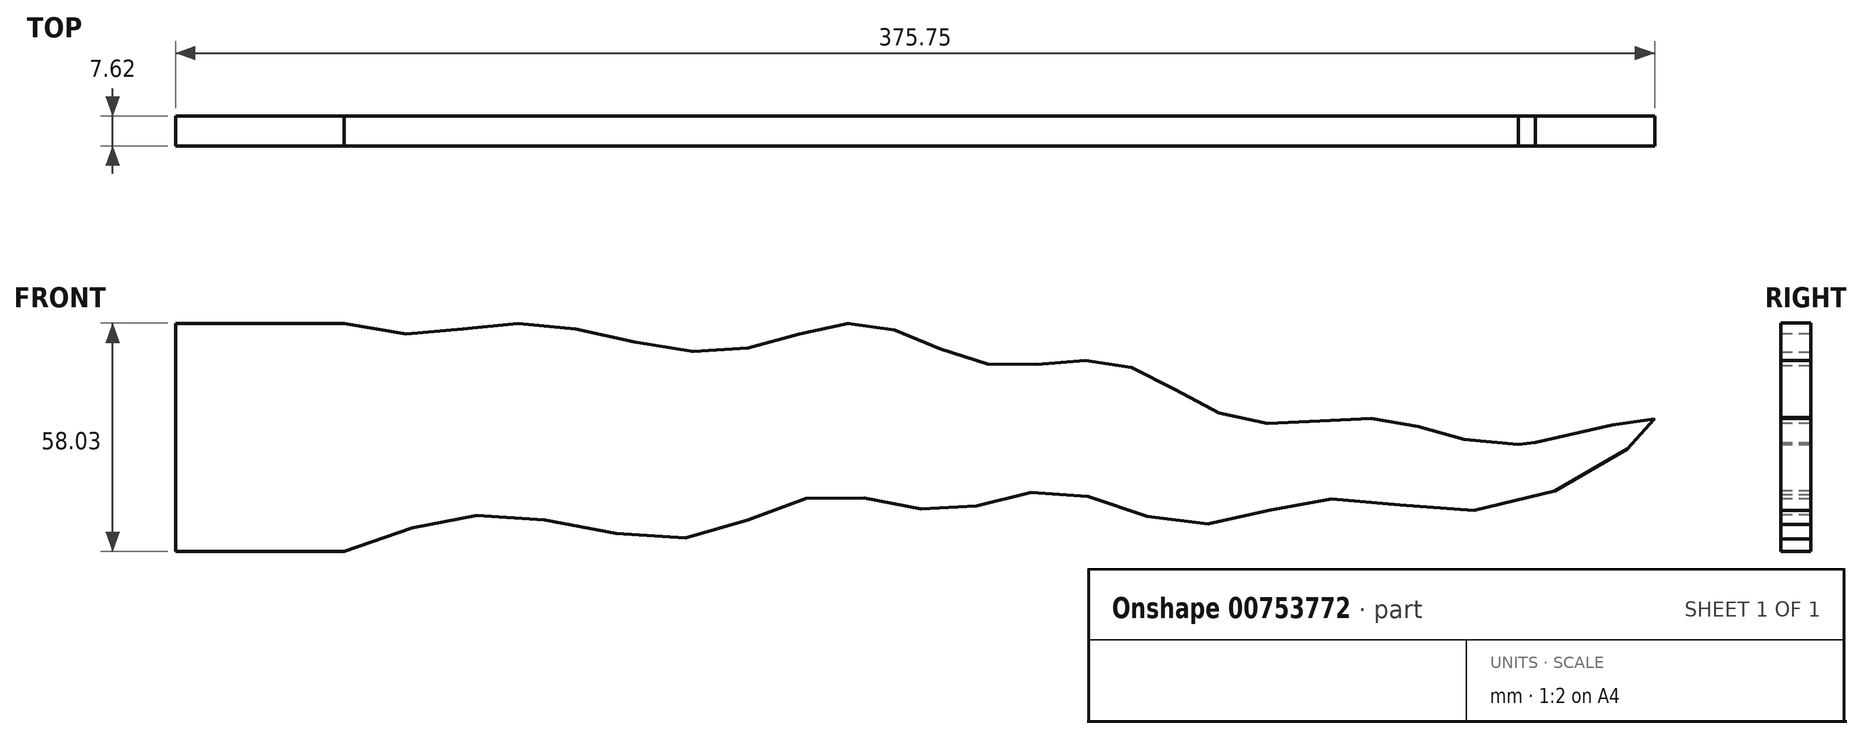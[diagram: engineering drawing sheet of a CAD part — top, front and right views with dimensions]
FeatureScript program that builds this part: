
annotation { "Feature Type Name" : "Feature", "Feature Type Description" : "" }
export const myFeature = defineFeature(function(context is Context, id is Id, definition is map)
    precondition{}
    {
        {
            var Q0;
            Q0=qCreatedBy(makeId("Front.planeOp"),FACE);
            var sketch = newSketch(context, id + "F0", { "sketchPlane" : qUnion([Q0])});
            skLineSegment(sketch, "E0.bottom", {"start": v(-130.14, 24.38) * mm, "end": v(-87.36, 24.38) * mm});
            skLineSegment(sketch, "E0.top", {"start": v(-130.14, -33.6) * mm, "end": v(-87.36, -33.6) * mm});
            skLineSegment(sketch, "E0.left", {"start": v(-130.14, 24.38) * mm, "end": v(-130.14, -33.6) * mm});
            skLineSegment(sketch, "E0.right", {"start": v(-87.36, 24.38) * mm, "end": v(-87.36, -33.6) * mm});
            skFitSpline(sketch, "E1", {"points": [v(-87.36, 24.38) * mm, v(-40.16, 24.38) * mm, v(7.86, 17.06) * mm, v(44.49, 24.38) * mm, v(76.3, 14.02) * mm, v(109.24, 14.24) * mm, v(139.64, 0) * mm, v(176.53, 0) * mm, v(210.97, -6.4) * mm, v(245.52, 0) * mm, v(211.78, -21.29) * mm, v(162.57, -20.33) * mm, v(127, -26.67) * mm, v(93.39, -18.18) * mm, v(65.16, -23.2) * mm, v(34.72, -19.34) * mm, v(0, -30.06) * mm, v(-45.62, -24.38) * mm, v(-87.36, -33.6) * mm], "startDerivative": vector(867.54, -301.74) * mm, "endDerivative": vector(-762.56, -288.29) * mm});
            skLineSegment(sketch, "E2.bottom", {"start": v(-130.14, 0) * mm, "end": v(-130.14, 0) * mm});
            skLineSegment(sketch, "E2.top", {"start": v(-130.14, -19) * mm, "end": v(-130.14, -19) * mm});
            skLineSegment(sketch, "E2.left", {"start": v(-130.14, 0) * mm, "end": v(-130.14, -19) * mm});
            skLineSegment(sketch, "E2.right", {"start": v(-130.14, 0) * mm, "end": v(-130.14, -19) * mm});
            skLineSegment(sketch, "E3", {"start": v(210.97, -6.4) * mm, "end": v(234, -3.99) * mm});
            skSolve(sketch);
        }
        {
            var Q0;
            Q0 = qSketchRegion(id + "F0", true);
            extrude(context, id + "F1", {"entities" : qUnion([Q0]), "depth" : 7.62 * mm, "offsetDistance" : 25.4 * mm});
        }
    });
